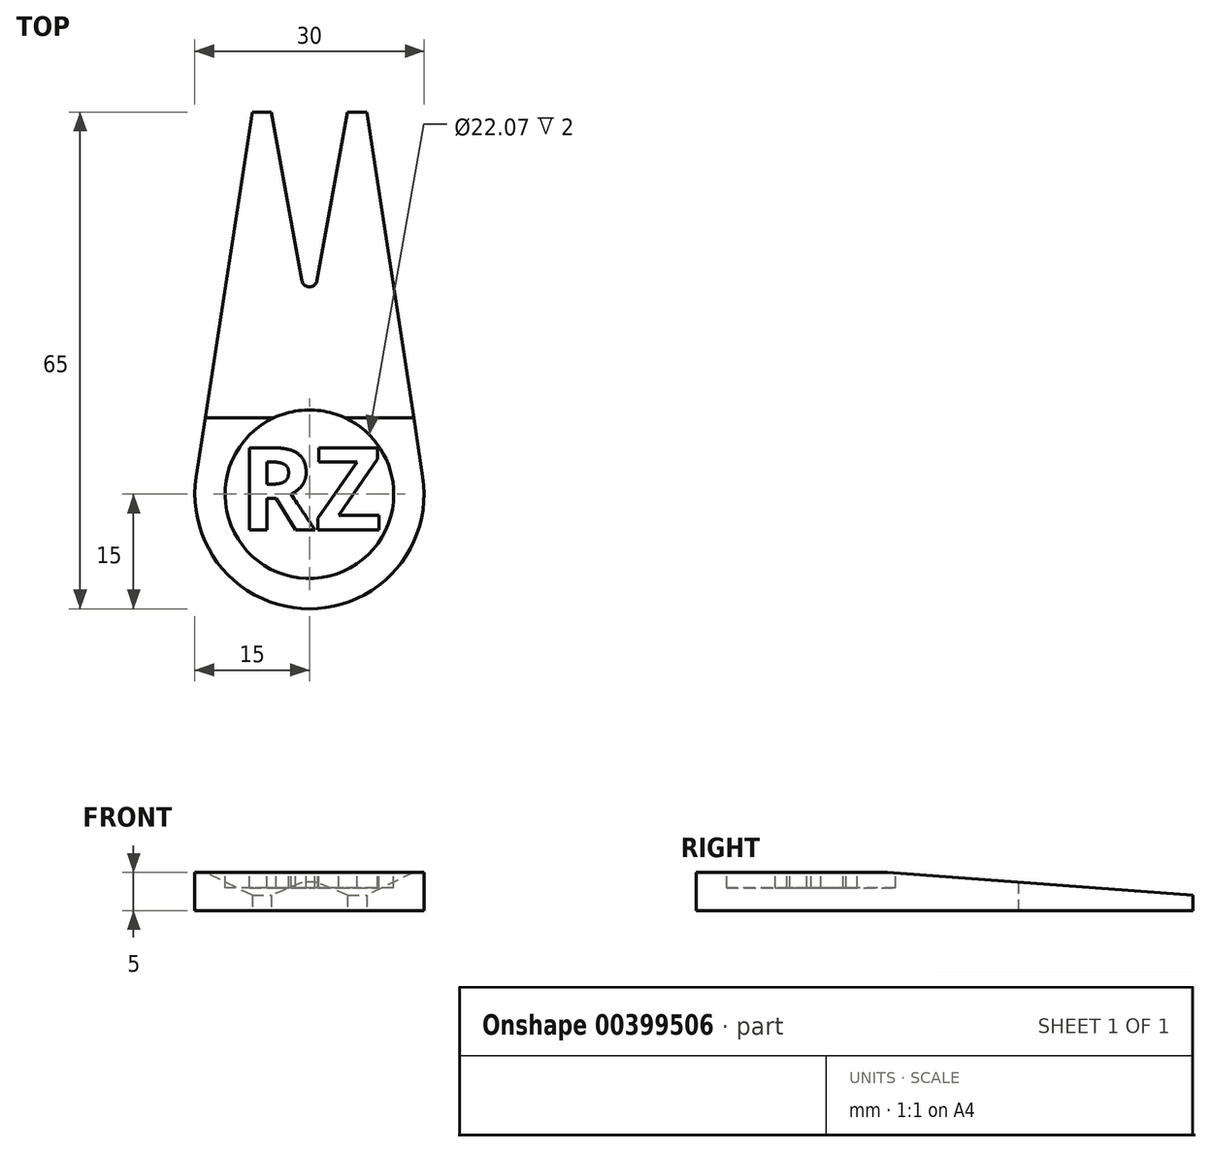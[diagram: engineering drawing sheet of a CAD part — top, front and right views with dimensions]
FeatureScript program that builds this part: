
annotation { "Feature Type Name" : "Feature", "Feature Type Description" : "" }
export const myFeature = defineFeature(function(context is Context, id is Id, definition is map)
    precondition{}
    {
        {
            var Q0;
            Q0=qCreatedBy(makeId("Top.planeOp"),FACE);
            var sketch = newSketch(context, id + "F0", { "sketchPlane" : qUnion([Q0])});
            skCircle(sketch, "E0", {"center": v(0, 0) * mm, "radius": 15 * mm});
            skLineSegment(sketch, "E1", {"start": v(-14.83, 2.28) * mm, "end": v(-7.5, 50) * mm});
            skLineSegment(sketch, "E2", {"start": v(-7.5, 50) * mm, "end": v(7.5, 50) * mm});
            skLineSegment(sketch, "E3", {"start": v(7.5, 50) * mm, "end": v(14.83, 2.28) * mm});
            skPoint(sketch, "E4", {"position": v(0, 50) * mm});
            skLineSegment(sketch, "E5", {"start": v(-5, 50) * mm, "end": v(-0.98, 27.95) * mm});
            skLineSegment(sketch, "E6", {"start": v(0.98, 27.95) * mm, "end": v(5, 50) * mm});
            skPoint(sketch, "E7.visualSharp", {"position": v(0, 22.55) * mm});
            skArc(sketch, "E7.filletArc", {"start": v(-0.98, 27.95) * mm, "mid": v(0, 27.13) * mm, "end": v(0.98, 27.95) * mm});
            skSolve(sketch);
        }
        {
            var Q0;
            {var subQ1=sQuery(id+"F0.wireOp",EDGE,"E1");Q0=makeQuery(id+"F0.imprint","IMPRINT",FACE,{"disambiguationData":[TD([[makeQuery(id+"F0.imprint","IMPRINT",EDGE,{"derivedFrom":subQ1}),-1.0]])]});}
            var Q1;
            {var subQ0=sQuery(id+"F0.wireOp",EDGE,"E0");var subQ1=makeQuery(id+"F0.imprint","INTERSECT",VERTEX,{"derivedFrom":[subQ0,sQuery(id+"F0.wireOp",EDGE,"E1")]});Q1=makeQuery(id+"F0.imprint","IMPRINT",FACE,{"disambiguationData":[TD([[makeQuery(id+"F0.imprint","IMPRINT",EDGE,{"disambiguationData":[TD([[subQ1,1.0]])],"derivedFrom":subQ0}),1.0]])]});}
            extrude(context, id + "F1", {"entities" : qUnion([Q0, Q1]), "depth" : 5 * mm});
        }
        {
            var Q0;
            {var subQ0=sQuery(id+"F0.wireOp",EDGE,"E2");Q0=makeQuery(id+"F1.opExtrude","CAP_EDGE",EDGE,{"disambiguationData":[OSD([subQ0]),TDD([makeQuery(id+"F0.imprint","IMPRINT",EDGE,{"disambiguationData":[TD([[makeQuery(id+"F0.imprint","INTERSECT",VERTEX,{"derivedFrom":[subQ0,sQuery(id+"F0.wireOp",EDGE,"E3")]}),1.0]])],"derivedFrom":subQ0})])],"isStart":false});}
            var Q1;
            {var subQ0=sQuery(id+"F0.wireOp",EDGE,"E2");Q1=makeQuery(id+"F1.opExtrude","CAP_EDGE",EDGE,{"disambiguationData":[OSD([subQ0]),TDD([makeQuery(id+"F0.imprint","IMPRINT",EDGE,{"disambiguationData":[TD([[makeQuery(id+"F0.imprint","INTERSECT",VERTEX,{"derivedFrom":[sQuery(id+"F0.wireOp",EDGE,"E1"),subQ0]}),-1.0]])],"derivedFrom":subQ0})])],"isStart":false});}
            chamfer(context, id + "F2", {"entities" : qUnion([Q0, Q1]), "chamferType" : ChamferType.TWO_OFFSETS, "width1" : 3 * mm, "oppositeDirection" : false, "width2" : 40 * mm, "tangentPropagation" : true});
        }
        {
            var Q0;
            Q0=makeQuery(id+"F1.opExtrude","CAP_FACE",FACE,{"disambiguationData":[OSD([sQuery(id+"F0.wireOp",EDGE,"E0"),sQuery(id+"F0.wireOp",EDGE,"E1"),sQuery(id+"F0.wireOp",EDGE,"E2"),sQuery(id+"F0.wireOp",EDGE,"E3"),sQuery(id+"F0.wireOp",EDGE,"E5"),sQuery(id+"F0.wireOp",EDGE,"E6"),sQuery(id+"F0.wireOp",EDGE,"E7.filletArc")])],"isStart":false});
            var sketch = newSketch(context, id + "F3", { "sketchPlane" : qUnion([Q0])});
            skCircle(sketch, "E8", {"center": v(0, 0) * mm, "radius": 11.04 * mm});
            skCircle(sketch, "E9", {"center": v(0, 0) * mm, "radius": 13.3 * mm, "construction": true});
            skText(sketch, "E10", { "text": "RZ", "fontName": "OpenSans-Bold.ttf"});
            const initialGuessF3  = {"E10": [-0.00919, -0.00465, 1, 0, 0.01082]};
            skSetInitialGuess(sketch, initialGuessF3);
            skSolve(sketch);
        }
        {
            var Q0;
            Q0 = qSketchRegion(id + "F3", true);
            var Q1;
            Q1=makeQuery(id+"F3.imprint","IMPRINT",FACE,{"disambiguationData":[TD([[makeQuery(id+"F3.imprint","IMPRINT",EDGE,{"derivedFrom":sQuery(id+"F3.wireOp",EDGE,"E10.sketch_text.stroke-0")}),1.0]])]});
            extrude(context, id + "F4", {"entities" : qUnion([Q0, Q1]), "operationType" : NewBodyOperationType.REMOVE, "oppositeDirection" : true, "depth" : 2 * mm});
        }
    });
